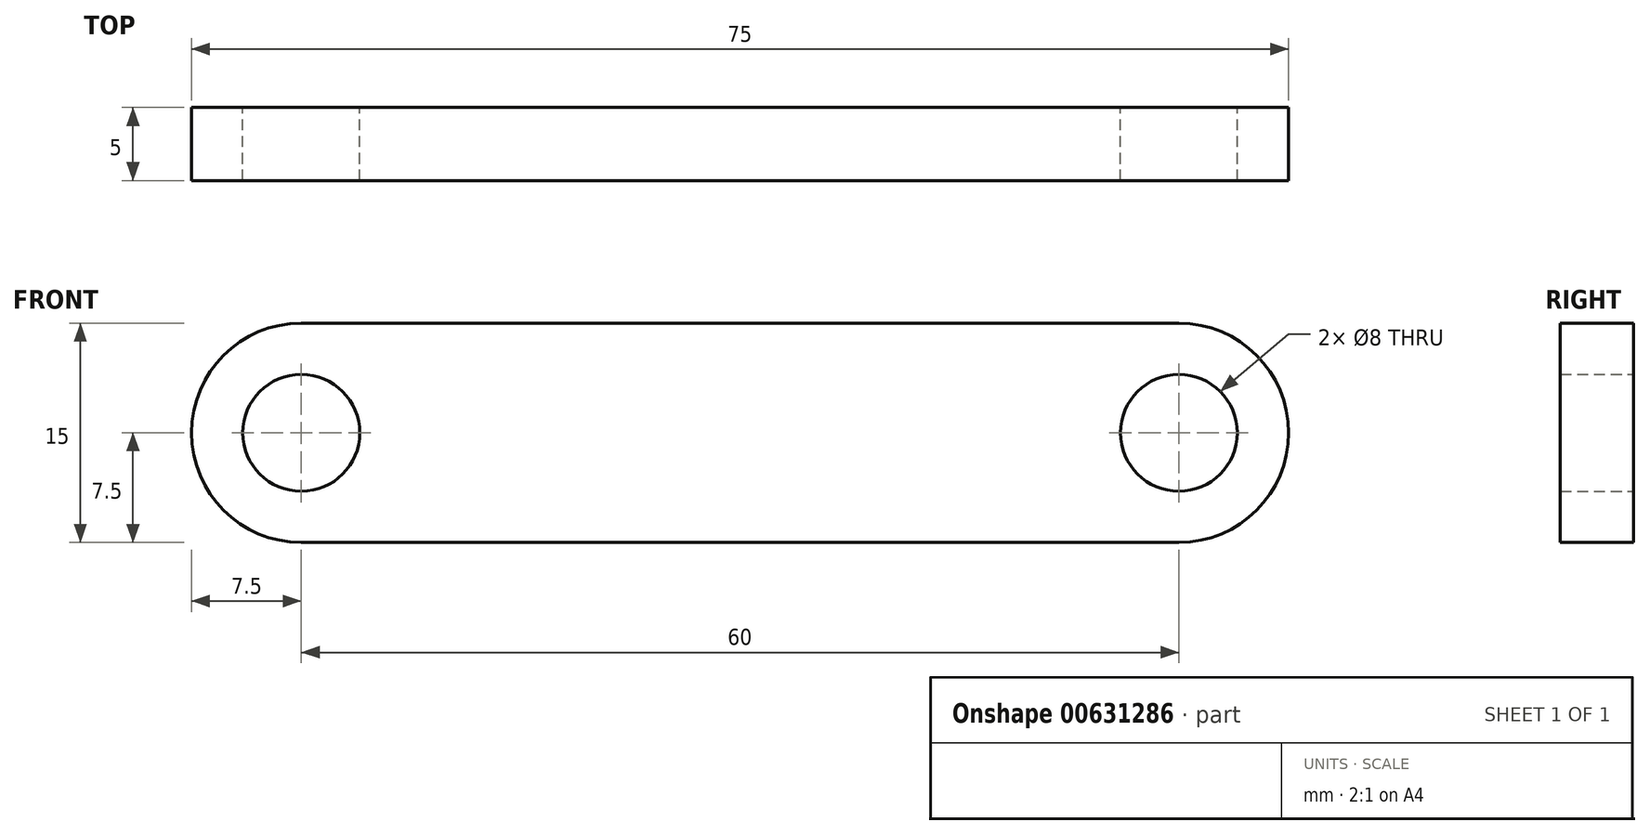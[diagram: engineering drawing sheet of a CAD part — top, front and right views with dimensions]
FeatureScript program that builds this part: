
annotation { "Feature Type Name" : "Feature", "Feature Type Description" : "" }
export const myFeature = defineFeature(function(context is Context, id is Id, definition is map)
    precondition{}
    {
        {
            var Q0;
            Q0=qCreatedBy(makeId("Front.planeOp"),FACE);
            var sketch = newSketch(context, id + "F0", { "sketchPlane" : qUnion([Q0])});
            skLineSegment(sketch, "E0", {"start": v(-46.42, 0) * mm, "end": v(52.4, 0) * mm, "construction": true});
            skArc(sketch, "E1", {"start": v(-30, 7.5) * mm, "mid": v(-37.5, 0) * mm, "end": v(-30, -7.5) * mm});
            skArc(sketch, "E2", {"start": v(30, -7.5) * mm, "mid": v(37.5, 0) * mm, "end": v(30, 7.5) * mm});
            skLineSegment(sketch, "E3", {"start": v(-30, 7.5) * mm, "end": v(30, 7.5) * mm});
            skLineSegment(sketch, "E4", {"start": v(30, -7.5) * mm, "end": v(-30, -7.5) * mm});
            skCircle(sketch, "E5", {"center": v(-30, 0) * mm, "radius": 4 * mm});
            skCircle(sketch, "E6", {"center": v(30, 0) * mm, "radius": 4 * mm});
            skSolve(sketch);
        }
        {
            var Q0;
            Q0 = qSketchRegion(id + "F0", true);
            extrude(context, id + "F1", {"entities" : qUnion([Q0]), "depth" : 5 * mm, "offsetDistance" : 25 * mm});
        }
    });
